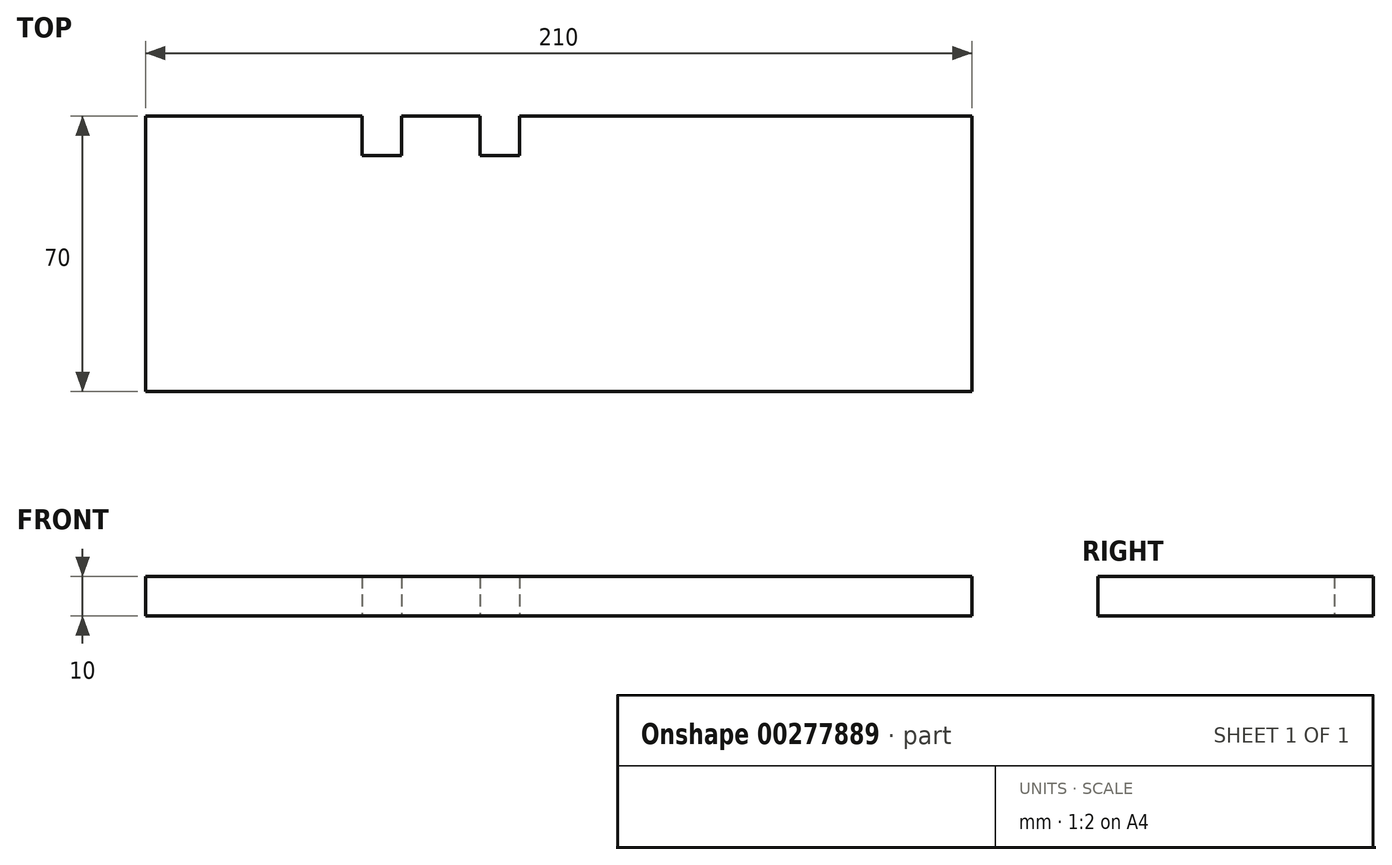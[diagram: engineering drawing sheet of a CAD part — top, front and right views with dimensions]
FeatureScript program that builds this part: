
annotation { "Feature Type Name" : "Feature", "Feature Type Description" : "" }
export const myFeature = defineFeature(function(context is Context, id is Id, definition is map)
    precondition{}
    {
        {
            var Q0;
            Q0=qCreatedBy(makeId("Top.planeOp"),FACE);
            var sketch = newSketch(context, id + "F0", { "sketchPlane" : qUnion([Q0])});
            skLineSegment(sketch, "E0", {"start": v(-0.56, -13.08) * mm, "end": v(-0.56, -23.08) * mm});
            skLineSegment(sketch, "E1", {"start": v(-0.56, -23.08) * mm, "end": v(9.44, -23.08) * mm});
            skLineSegment(sketch, "E2", {"start": v(9.44, -23.08) * mm, "end": v(9.44, -13.08) * mm});
            skLineSegment(sketch, "E3", {"start": v(9.44, -13.08) * mm, "end": v(29.44, -13.08) * mm});
            skLineSegment(sketch, "E4", {"start": v(29.44, -13.08) * mm, "end": v(29.44, -23.08) * mm});
            skLineSegment(sketch, "E5", {"start": v(29.44, -23.08) * mm, "end": v(39.44, -23.08) * mm});
            skLineSegment(sketch, "E6", {"start": v(39.44, -23.08) * mm, "end": v(39.44, -13.08) * mm});
            skLineSegment(sketch, "E7", {"start": v(39.44, -13.08) * mm, "end": v(154.44, -13.08) * mm});
            skLineSegment(sketch, "E8", {"start": v(154.44, -13.08) * mm, "end": v(154.44, -83.08) * mm});
            skLineSegment(sketch, "E9", {"start": v(154.44, -83.08) * mm, "end": v(-55.56, -83.08) * mm});
            skLineSegment(sketch, "E10", {"start": v(-55.56, -83.08) * mm, "end": v(-55.56, -13.08) * mm});
            skLineSegment(sketch, "E11", {"start": v(-55.56, -13.08) * mm, "end": v(-0.56, -13.08) * mm});
            skSolve(sketch);
        }
        {
            var Q0;
            Q0=qSketchRegion(id+"F0",true);
            extrude(context, id + "F1", {"entities" : qUnion([Q0]), "depth" : 10 * mm});
        }
    });
